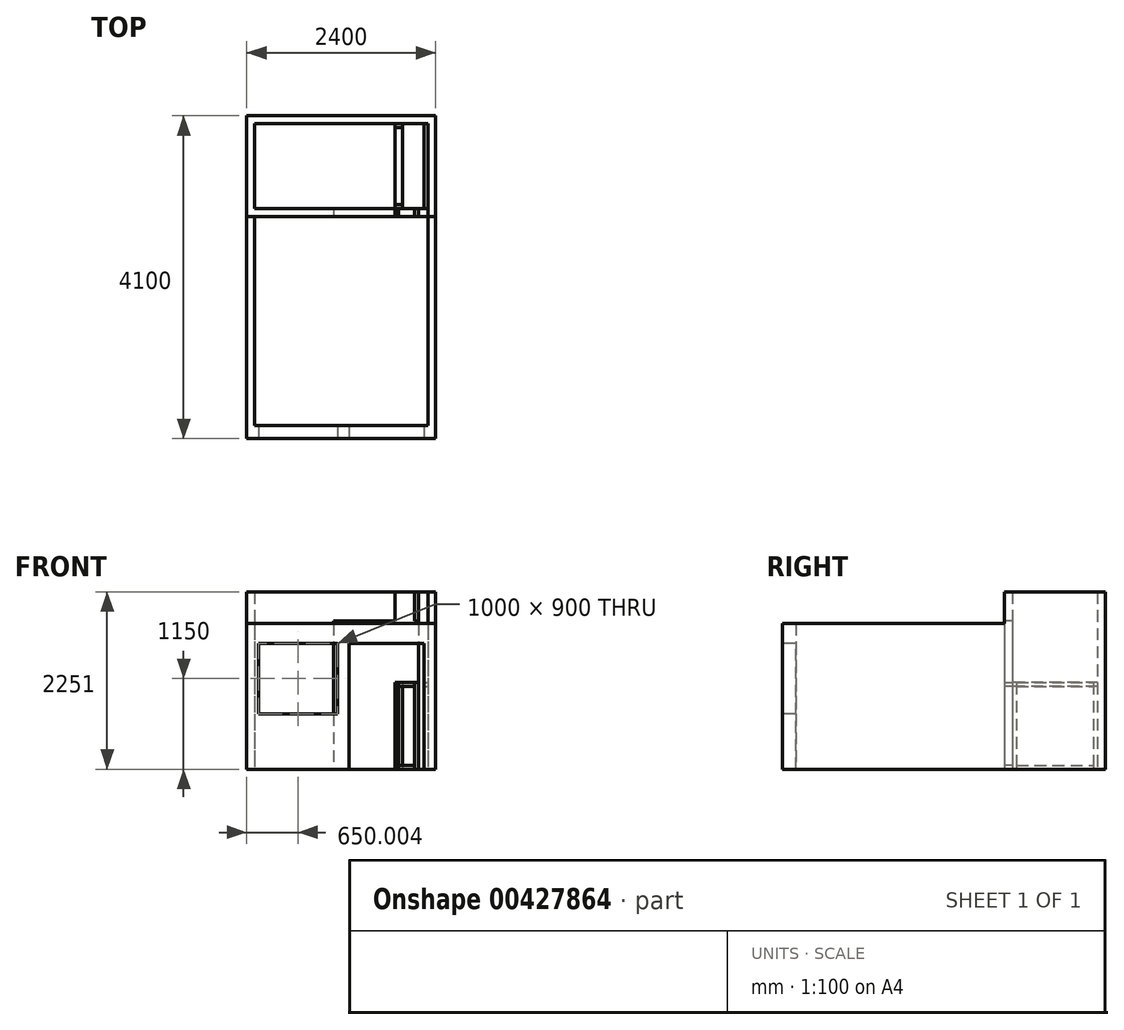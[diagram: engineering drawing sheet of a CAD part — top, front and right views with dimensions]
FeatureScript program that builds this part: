
annotation { "Feature Type Name" : "Feature", "Feature Type Description" : "" }
export const myFeature = defineFeature(function(context is Context, id is Id, definition is map)
    precondition{}
    {
        {
            var Q0;
            Q0=qCreatedBy(makeId("Top.planeOp"),FACE);
            var sketch = newSketch(context, id + "F0", { "sketchPlane" : qUnion([Q0])});
            skLineSegment(sketch, "E0.bottom", {"start": v(-1154.58, 4000) * mm, "end": v(1045.42, 4000) * mm});
            skLineSegment(sketch, "E0.top", {"start": v(-1154.58, 167.16) * mm, "end": v(1045.42, 167.16) * mm});
            skLineSegment(sketch, "E0.left", {"start": v(-1154.58, 4000) * mm, "end": v(-1154.58, 167.16) * mm});
            skLineSegment(sketch, "E0.right", {"start": v(1045.42, 4000) * mm, "end": v(1045.42, 167.16) * mm});
            skLineSegment(sketch, "E1.bottom", {"start": v(-1154.58, 2920) * mm, "end": v(-154.58, 2920) * mm});
            skLineSegment(sketch, "E1.top", {"start": v(-1154.58, 2820) * mm, "end": v(-154.58, 2820) * mm});
            skLineSegment(sketch, "E1.left", {"start": v(-1154.58, 2920) * mm, "end": v(-1154.58, 2820) * mm});
            skLineSegment(sketch, "E1.right", {"start": v(-154.58, 2920) * mm, "end": v(-154.58, 2820) * mm});
            skLineSegment(sketch, "E2.bottom", {"start": v(-1254.58, 4100) * mm, "end": v(1145.42, 4100) * mm});
            skLineSegment(sketch, "E2.top", {"start": v(-1254.58, 0) * mm, "end": v(1145.42, 0) * mm});
            skLineSegment(sketch, "E2.left", {"start": v(-1254.58, 4100) * mm, "end": v(-1254.58, 0) * mm});
            skLineSegment(sketch, "E2.right", {"start": v(1145.42, 4100) * mm, "end": v(1145.42, 0) * mm});
            skLineSegment(sketch, "E3.bottom", {"start": v(-154.58, 2820) * mm, "end": v(1045.42, 2820) * mm});
            skLineSegment(sketch, "E3.top", {"start": v(-154.58, 2920) * mm, "end": v(1045.42, 2920) * mm});
            skLineSegment(sketch, "E3.left", {"start": v(-154.58, 2820) * mm, "end": v(-154.58, 2920) * mm});
            skLineSegment(sketch, "E3.right", {"start": v(1045.42, 2820) * mm, "end": v(1045.42, 2920) * mm});
            skLineSegment(sketch, "E4", {"start": v(-1154.58, 2820) * mm, "end": v(-1254.58, 2820) * mm});
            skLineSegment(sketch, "E5", {"start": v(1045.42, 2820) * mm, "end": v(1145.42, 2820) * mm});
            skLineSegment(sketch, "E6", {"start": v(925.42, 2920) * mm, "end": v(925.42, 2820) * mm});
            skLineSegment(sketch, "E7", {"start": v(1045.42, 4000) * mm, "end": v(995.42, 4000) * mm});
            skLineSegment(sketch, "E8", {"start": v(625.42, 4000) * mm, "end": v(727.44, 4000) * mm});
            skLineSegment(sketch, "E9", {"start": v(725.42, 2920) * mm, "end": v(625.42, 2920) * mm});
            skLineSegment(sketch, "E10", {"start": v(625.42, 2920) * mm, "end": v(725.42, 2920) * mm});
            skLineSegment(sketch, "E11", {"start": v(625.42, 2920) * mm, "end": v(625.42, 2820) * mm});
            skLineSegment(sketch, "E12", {"start": v(625.42, 4000) * mm, "end": v(625.42, 2920) * mm});
            skLineSegment(sketch, "E13", {"start": v(995.42, 4000) * mm, "end": v(995.42, 2920) * mm});
            skLineSegment(sketch, "E14", {"start": v(725.42, 2920) * mm, "end": v(725.42, 4000) * mm});
            skLineSegment(sketch, "E15", {"start": v(725.42, 2920) * mm, "end": v(725.42, 2820) * mm});
            skLineSegment(sketch, "E16", {"start": v(725.42, 3950) * mm, "end": v(625.42, 3950) * mm});
            skLineSegment(sketch, "E17", {"start": v(1045.42, 3900) * mm, "end": v(995.42, 3900) * mm});
            skLineSegment(sketch, "E18", {"start": v(675.42, 2920) * mm, "end": v(675.42, 2820) * mm});
            skLineSegment(sketch, "E19", {"start": v(675.42, 2820) * mm, "end": v(875.42, 2820) * mm});
            skLineSegment(sketch, "E20", {"start": v(875.42, 2820) * mm, "end": v(875.42, 2920) * mm});
            skLineSegment(sketch, "E21", {"start": v(725.42, 2970) * mm, "end": v(625.42, 2970) * mm});
            skSolve(sketch);
        }
        {
            var Q0;
            {var subQ17=sQuery(id+"F0.wireOp",EDGE,"E2.bottom");var subQ24=sQuery(id+"F0.wireOp",EDGE,"E0.top");Q0=qUnion([makeQuery(id+"F0.imprint","IMPRINT",FACE,{"disambiguationData":[TD([[makeQuery(id+"F0.imprint","IMPRINT",EDGE,{"derivedFrom":subQ24}),-1.0]])]}),makeQuery(id+"F0.imprint","IMPRINT",FACE,{"disambiguationData":[TD([[makeQuery(id+"F0.imprint","IMPRINT",EDGE,{"derivedFrom":subQ17}),-1.0]])]})]);}
            var Q1;
            {var subQ2=sQuery(id+"F0.wireOp",EDGE,"E1.bottom");Q1=makeQuery(id+"F0.imprint","IMPRINT",FACE,{"disambiguationData":[TD([[makeQuery(id+"F0.imprint","IMPRINT",EDGE,{"derivedFrom":subQ2}),-1.0]])]});}
            var Q2;
            {var subQ4=sQuery(id+"F0.wireOp",EDGE,"E6");Q2=makeQuery(id+"F0.imprint","IMPRINT",FACE,{"disambiguationData":[TD([[makeQuery(id+"F0.imprint","IMPRINT",EDGE,{"derivedFrom":subQ4}),1.0]])]});}
            extrude(context, id + "F1", {"entities" : qUnion([Q0, Q1, Q2]), "depth" : 2250 * mm, "offsetDistance" : 25 * mm});
        }
        {
            var Q0;
            {var subQ0=sQuery(id+"F0.wireOp",EDGE,"E1.right");var subQ7=sQuery(id+"F0.wireOp",EDGE,"E11");var subQ10=makeQuery(id+"F0.imprint","IMPRINT",EDGE,{"derivedFrom":subQ7});var subQ11=sQuery(id+"F0.wireOp",EDGE,"E6");Q0=qUnion([makeQuery(id+"F0.imprint","IMPRINT",FACE,{"disambiguationData":[TD([[makeQuery(id+"F0.imprint","IMPRINT",EDGE,{"derivedFrom":subQ11}),-1.0]])]}),makeQuery(id+"F0.imprint","IMPRINT",FACE,{"disambiguationData":[TD([[subQ10,-1.0]])]}),makeQuery(id+"F0.imprint","IMPRINT",FACE,{"disambiguationData":[TD([[makeQuery(id+"F0.imprint","IMPRINT",EDGE,{"derivedFrom":subQ0}),1.0]])]})]);}
            extrude(context, id + "F2", {"entities" : qUnion([Q0]), "operationType" : NewBodyOperationType.ADD, "depth" : 2250 * mm, "offsetDistance" : 25 * mm, "hasSecondDirection" : true, "secondDirectionOppositeDirection" : false, "secondDirectionDepth" : (2280 - 400) * mm});
        }
        {
            var Q0;
            {var subQ2=sQuery(id+"F0.wireOp",EDGE,"E0.top");Q0=makeQuery(id+"F0.imprint","IMPRINT",FACE,{"disambiguationData":[TD([[makeQuery(id+"F0.imprint","IMPRINT",EDGE,{"derivedFrom":subQ2}),-1.0]])]});}
            var Q1;
            Q1=makeQuery(id+"F1.opExtrude","SWEPT_BODY",BODY,{"disambiguationData":[OSD([sQuery(id+"F0.wireOp",EDGE,"E0.bottom"),sQuery(id+"F0.wireOp",EDGE,"E0.top"),sQuery(id+"F0.wireOp",EDGE,"E0.left"),sQuery(id+"F0.wireOp",EDGE,"E0.right"),sQuery(id+"F0.wireOp",EDGE,"E1.bottom"),sQuery(id+"F0.wireOp",EDGE,"E1.top"),sQuery(id+"F0.wireOp",EDGE,"E1.right"),sQuery(id+"F0.wireOp",EDGE,"E2.bottom"),sQuery(id+"F0.wireOp",EDGE,"E2.top"),sQuery(id+"F0.wireOp",EDGE,"E2.left"),sQuery(id+"F0.wireOp",EDGE,"E2.right"),sQuery(id+"F0.wireOp",EDGE,"E3.bottom"),sQuery(id+"F0.wireOp",EDGE,"E3.top"),sQuery(id+"F0.wireOp",EDGE,"E6")])]});
            extrude(context, id + "F3", {"entities" : qUnion([Q0]), "operationType" : NewBodyOperationType.REMOVE, "endBound" : BoundingType.UP_TO_BODY, "depth" : 2430 * mm, "endBoundEntityBody" : qUnion([Q1]), "offsetDistance" : 25 * mm, "hasSecondDirection" : true, "secondDirectionOppositeDirection" : false, "secondDirectionDepth" : 1850 * mm});
        }
        {
            var Q0;
            Q0=makeQuery(id+"F1.opExtrude","SWEPT_FACE",FACE,{"disambiguationData":[OSD([sQuery(id+"F0.wireOp",EDGE,"E2.top")])]});
            var sketch = newSketch(context, id + "F4", { "sketchPlane" : qUnion([Q0])});
            skLineSegment(sketch, "E22.bottom", {"start": v(995.42, 0) * mm, "end": v(45.42, 0) * mm});
            skLineSegment(sketch, "E22.top", {"start": v(995.42, 1600) * mm, "end": v(45.42, 1600) * mm});
            skLineSegment(sketch, "E22.left", {"start": v(995.42, 0) * mm, "end": v(995.42, 1600) * mm});
            skLineSegment(sketch, "E22.right", {"start": v(45.42, 0) * mm, "end": v(45.42, 1600) * mm});
            skLineSegment(sketch, "E23.bottom", {"start": v(-1104.58, 1600) * mm, "end": v(-104.58, 1600) * mm});
            skLineSegment(sketch, "E23.top", {"start": v(-1104.58, 700) * mm, "end": v(-104.58, 700) * mm});
            skLineSegment(sketch, "E23.left", {"start": v(-1104.58, 1600) * mm, "end": v(-1104.58, 700) * mm});
            skLineSegment(sketch, "E23.right", {"start": v(-104.58, 1600) * mm, "end": v(-104.58, 700) * mm});
            skSolve(sketch);
        }
        {
            var Q0;
            Q0=makeQuery(id+"F4.imprint","IMPRINT",FACE,{"disambiguationData":[TD([[makeQuery(id+"F4.imprint","IMPRINT",EDGE,{"derivedFrom":sQuery(id+"F4.wireOp",EDGE,"E23.bottom")}),-1.0]])]});
            var Q1;
            Q1=makeQuery(id+"F4.imprint","IMPRINT",FACE,{"disambiguationData":[TD([[makeQuery(id+"F4.imprint","IMPRINT",EDGE,{"derivedFrom":sQuery(id+"F4.wireOp",EDGE,"E22.bottom")}),1.0]])]});
            var Q2;
            Q2=makeQuery(id+"F1.opExtrude","SWEPT_FACE",FACE,{"disambiguationData":[OSD([sQuery(id+"F0.wireOp",EDGE,"E0.top")])]});
            extrude(context, id + "F5", {"entities" : qUnion([Q0, Q1]), "operationType" : NewBodyOperationType.REMOVE, "endBound" : BoundingType.UP_TO_SURFACE, "oppositeDirection" : true, "depth" : 25 * mm, "endBoundEntityFace" : qUnion([Q2]), "offsetDistance" : 25 * mm});
        }
        {
            var Q0;
            {var subQ0=sQuery(id+"F0.wireOp",EDGE,"E18");Q0=makeQuery(id+"F0.imprint","IMPRINT",FACE,{"disambiguationData":[TD([[makeQuery(id+"F0.imprint","IMPRINT",EDGE,{"derivedFrom":subQ0}),1.0]])]});}
            var Q1;
            {var subQ0=sQuery(id+"F0.wireOp",EDGE,"E15");Q1=makeQuery(id+"F0.imprint","IMPRINT",FACE,{"disambiguationData":[TD([[makeQuery(id+"F0.imprint","IMPRINT",EDGE,{"derivedFrom":subQ0}),1.0]])]});}
            extrude(context, id + "F6", {"entities" : qUnion([Q0, Q1]), "depth" : 50 * mm, "offsetDistance" : 25 * mm});
        }
        {
            var Q0;
            {var subQ4=sQuery(id+"F0.wireOp",EDGE,"E6");Q0=makeQuery(id+"F0.imprint","IMPRINT",FACE,{"disambiguationData":[TD([[makeQuery(id+"F0.imprint","IMPRINT",EDGE,{"derivedFrom":subQ4}),1.0]])]});}
            extrude(context, id + "F7", {"entities" : qUnion([Q0]), "depth" : 2251 * mm, "offsetDistance" : 25 * mm});
        }
        {
            var Q0;
            {var subQ5=sQuery(id+"F0.wireOp",EDGE,"E16");Q0=makeQuery(id+"F0.imprint","IMPRINT",FACE,{"disambiguationData":[TD([[makeQuery(id+"F0.imprint","IMPRINT",EDGE,{"derivedFrom":subQ5}),-1.0]])]});}
            extrude(context, id + "F8", {"entities" : qUnion([Q0]), "depth" : 1100 * mm, "offsetDistance" : 25 * mm});
        }
        {
            var Q0;
            {var subQ5=sQuery(id+"F0.wireOp",EDGE,"E16");Q0=makeQuery(id+"F0.imprint","IMPRINT",FACE,{"disambiguationData":[TD([[makeQuery(id+"F0.imprint","IMPRINT",EDGE,{"derivedFrom":subQ5}),1.0]])]});}
            extrude(context, id + "F9", {"entities" : qUnion([Q0]), "depth" : 50 * mm, "offsetDistance" : 25 * mm});
        }
        {
            var Q0;
            {var subQ5=sQuery(id+"F0.wireOp",EDGE,"E16");Q0=makeQuery(id+"F0.imprint","IMPRINT",FACE,{"disambiguationData":[TD([[makeQuery(id+"F0.imprint","IMPRINT",EDGE,{"derivedFrom":subQ5}),1.0]])]});}
            var Q1;
            Q1=makeQuery(id+"F8.opExtrude","CAP_FACE",FACE,{"disambiguationData":[OSD([sQuery(id+"F0.wireOp",EDGE,"E0.bottom"),sQuery(id+"F0.wireOp",EDGE,"E12"),sQuery(id+"F0.wireOp",EDGE,"E14"),sQuery(id+"F0.wireOp",EDGE,"E16")])],"isStart":false});
            var Q2;
            Q2=makeQuery(id+"F8.opExtrude","CAP_FACE",FACE,{"disambiguationData":[OSD([sQuery(id+"F0.wireOp",EDGE,"E0.bottom"),sQuery(id+"F0.wireOp",EDGE,"E12"),sQuery(id+"F0.wireOp",EDGE,"E14"),sQuery(id+"F0.wireOp",EDGE,"E16")])],"isStart":false});
            extrude(context, id + "F10", {"entities" : qUnion([Q0]), "endBound" : BoundingType.UP_TO_SURFACE, "depth" : 662 * mm, "endBoundEntityFace" : qUnion([Q1]), "offsetDistance" : 50 * mm, "offsetOppositeDirection" : true, "hasSecondDirection" : true, "secondDirectionOppositeDirection" : false, "secondDirectionDepth" : (1100 - 50) * mm, "secondDirectionBoundEntityFace" : qUnion([Q2])});
        }
        {
            var Q0;
            {var subQ0=sQuery(id+"F0.wireOp",EDGE,"E18");Q0=makeQuery(id+"F0.imprint","IMPRINT",FACE,{"disambiguationData":[TD([[makeQuery(id+"F0.imprint","IMPRINT",EDGE,{"derivedFrom":subQ0}),1.0]])]});}
            var Q1;
            {var subQ0=sQuery(id+"F0.wireOp",EDGE,"E15");Q1=makeQuery(id+"F0.imprint","IMPRINT",FACE,{"disambiguationData":[TD([[makeQuery(id+"F0.imprint","IMPRINT",EDGE,{"derivedFrom":subQ0}),1.0]])]});}
            var Q2;
            Q2=makeQuery(id+"F10.opExtrude","CAP_FACE",FACE,{"disambiguationData":[OSD([sQuery(id+"F0.wireOp",EDGE,"E3.top"),sQuery(id+"F0.wireOp",EDGE,"E12"),sQuery(id+"F0.wireOp",EDGE,"E14"),sQuery(id+"F0.wireOp",EDGE,"E16")])],"isStart":false});
            extrude(context, id + "F11", {"entities" : qUnion([Q0, Q1]), "endBound" : BoundingType.UP_TO_SURFACE, "depth" : 25 * mm, "endBoundEntityFace" : qUnion([Q2]), "offsetDistance" : 25 * mm, "hasSecondDirection" : true, "secondDirectionOppositeDirection" : false, "secondDirectionDepth" : 1050 * mm});
        }
        {
            var Q0;
            {var subQ5=sQuery(id+"F0.wireOp",EDGE,"E17");Q0=makeQuery(id+"F0.imprint","IMPRINT",FACE,{"disambiguationData":[TD([[makeQuery(id+"F0.imprint","IMPRINT",EDGE,{"derivedFrom":subQ5}),-1.0]])]});}
            var Q1;
            {var subQ3=sQuery(id+"F0.wireOp",EDGE,"E17");Q1=makeQuery(id+"F0.imprint","IMPRINT",FACE,{"disambiguationData":[TD([[makeQuery(id+"F0.imprint","IMPRINT",EDGE,{"derivedFrom":subQ3}),1.0]])]});}
            var Q2;
            Q2=makeQuery(id+"F10.opExtrude","CAP_FACE",FACE,{"disambiguationData":[OSD([sQuery(id+"F0.wireOp",EDGE,"E0.bottom"),sQuery(id+"F0.wireOp",EDGE,"E3.top"),sQuery(id+"F0.wireOp",EDGE,"E12"),sQuery(id+"F0.wireOp",EDGE,"E14")])],"isStart":false});
            extrude(context, id + "F12", {"entities" : qUnion([Q0, Q1]), "endBound" : BoundingType.UP_TO_SURFACE, "depth" : 468 * mm, "endBoundEntityFace" : qUnion([Q2]), "offsetDistance" : 25 * mm, "hasSecondDirection" : true, "secondDirectionOppositeDirection" : false, "secondDirectionDepth" : 1050 * mm});
        }
        {
            var Q0;
            {var subQ2=sQuery(id+"F0.wireOp",EDGE,"E11");Q0=makeQuery(id+"F0.imprint","IMPRINT",FACE,{"disambiguationData":[TD([[makeQuery(id+"F0.imprint","IMPRINT",EDGE,{"derivedFrom":subQ2}),1.0]])]});}
            var Q1;
            {var subQ0=sQuery(id+"F0.wireOp",EDGE,"E6");Q1=makeQuery(id+"F0.imprint","IMPRINT",FACE,{"disambiguationData":[TD([[makeQuery(id+"F0.imprint","IMPRINT",EDGE,{"derivedFrom":subQ0}),-1.0]])]});}
            var Q2;
            Q2=makeQuery(id+"F8.opExtrude","CAP_FACE",FACE,{"disambiguationData":[OSD([sQuery(id+"F0.wireOp",EDGE,"E0.bottom"),sQuery(id+"F0.wireOp",EDGE,"E12"),sQuery(id+"F0.wireOp",EDGE,"E14"),sQuery(id+"F0.wireOp",EDGE,"E16")])],"isStart":false});
            var Q3;
            Q3=makeQuery(id+"F6.opExtrude","CAP_FACE",FACE,{"disambiguationData":[OSD([sQuery(id+"F0.wireOp",EDGE,"E3.bottom"),sQuery(id+"F0.wireOp",EDGE,"E3.top"),sQuery(id+"F0.wireOp",EDGE,"E6"),sQuery(id+"F0.wireOp",EDGE,"E11")])],"isStart":false});
            var Q4;
            Q4=makeQuery(id+"F6.opExtrude","SWEPT_BODY",BODY,{"disambiguationData":[OSD([sQuery(id+"F0.wireOp",EDGE,"E3.bottom"),sQuery(id+"F0.wireOp",EDGE,"E3.top"),sQuery(id+"F0.wireOp",EDGE,"E6"),sQuery(id+"F0.wireOp",EDGE,"E11")])]});
            extrude(context, id + "F13", {"entities" : qUnion([Q0, Q1]), "endBound" : BoundingType.UP_TO_SURFACE, "depth" : 25 * mm, "endBoundEntityFace" : qUnion([Q2]), "offsetDistance" : 25 * mm});
        }
        {
            var Q0;
            {var subQ0=sQuery(id+"F0.wireOp",EDGE,"E21");Q0=makeQuery(id+"F0.imprint","IMPRINT",FACE,{"disambiguationData":[TD([[makeQuery(id+"F0.imprint","IMPRINT",EDGE,{"derivedFrom":subQ0}),1.0]])]});}
            var Q1;
            Q1=makeQuery(id+"F8.opExtrude","CAP_FACE",FACE,{"disambiguationData":[OSD([sQuery(id+"F0.wireOp",EDGE,"E0.bottom"),sQuery(id+"F0.wireOp",EDGE,"E12"),sQuery(id+"F0.wireOp",EDGE,"E14"),sQuery(id+"F0.wireOp",EDGE,"E16")])],"isStart":false});
            var Q2;
            Q2=makeQuery(id+"F9.opExtrude","CAP_FACE",FACE,{"disambiguationData":[OSD([sQuery(id+"F0.wireOp",EDGE,"E3.top"),sQuery(id+"F0.wireOp",EDGE,"E12"),sQuery(id+"F0.wireOp",EDGE,"E14"),sQuery(id+"F0.wireOp",EDGE,"E16")])],"isStart":false});
            extrude(context, id + "F14", {"entities" : qUnion([Q0]), "endBound" : BoundingType.UP_TO_SURFACE, "depth" : 25 * mm, "endBoundEntityFace" : qUnion([Q1]), "offsetDistance" : 25 * mm});
        }
    });
